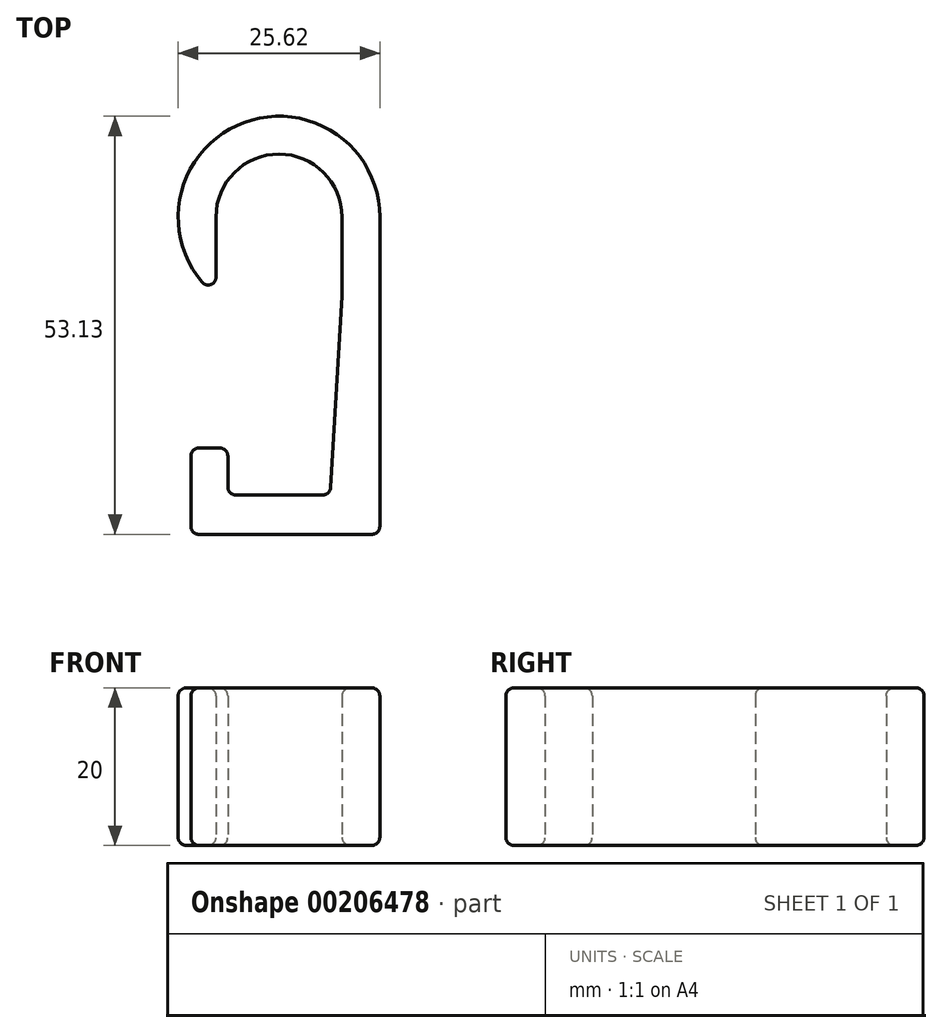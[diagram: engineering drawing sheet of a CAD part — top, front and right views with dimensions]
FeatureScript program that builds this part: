
annotation { "Feature Type Name" : "Feature", "Feature Type Description" : "" }
export const myFeature = defineFeature(function(context is Context, id is Id, definition is map)
    precondition{}
    {
        {
            var Q0;
            Q0=qCreatedBy(makeId("Top.planeOp"),FACE);
            var sketch = newSketch(context, id + "F0", { "sketchPlane" : qUnion([Q0])});
            skArc(sketch, "E0", {"start": v(8, 0) * mm, "mid": v(0, 8) * mm, "end": v(-8, 0) * mm});
            skArc(sketch, "E1", {"start": v(12.8, 0) * mm, "mid": v(-5.55, 11.54) * mm, "end": v(-8, -10) * mm});
            skLineSegment(sketch, "E2", {"start": v(-8, 0) * mm, "end": v(-8, -10) * mm});
            skLineSegment(sketch, "E3", {"start": v(8, 0) * mm, "end": v(8, -10) * mm});
            skLineSegment(sketch, "E4", {"start": v(0, -35.32) * mm, "end": v(6.5, -35.32) * mm});
            skLineSegment(sketch, "E5", {"start": v(0, -35.32) * mm, "end": v(-6.5, -35.32) * mm});
            skLineSegment(sketch, "E6", {"start": v(8, -10) * mm, "end": v(6.5, -35.32) * mm});
            skLineSegment(sketch, "E7", {"start": v(12.8, 0) * mm, "end": v(12.8, -40.32) * mm});
            skLineSegment(sketch, "E8", {"start": v(12.8, -40.32) * mm, "end": v(-11.2, -40.32) * mm});
            skLineSegment(sketch, "E9", {"start": v(-11.2, -29.34) * mm, "end": v(-6.5, -29.34) * mm});
            skLineSegment(sketch, "E10", {"start": v(-6.5, -29.34) * mm, "end": v(-6.5, -35.32) * mm});
            skLineSegment(sketch, "E11", {"start": v(-11.2, -40.32) * mm, "end": v(-11.2, -29.34) * mm});
            skSolve(sketch);
        }
        {
            var Q0;
            Q0=makeQuery(id+"F0.imprint","IMPRINT",FACE,{"disambiguationData":[TD([[makeQuery(id+"F0.imprint","IMPRINT",EDGE,{"derivedFrom":sQuery(id+"F0.wireOp",EDGE,"E0")}),-1.0]])]});
            extrude(context, id + "F1", {"entities" : qUnion([Q0]), "depth" : 20 * mm});
        }
        {
            var Q0;
            Q0=makeQuery(id+"F1.opExtrude","CAP_FACE",FACE,{"disambiguationData":[OSD([sQuery(id+"F0.wireOp",EDGE,"E0"),sQuery(id+"F0.wireOp",EDGE,"E1"),sQuery(id+"F0.wireOp",EDGE,"E2"),sQuery(id+"F0.wireOp",EDGE,"E3"),sQuery(id+"F0.wireOp",EDGE,"E4"),sQuery(id+"F0.wireOp",EDGE,"E5"),sQuery(id+"F0.wireOp",EDGE,"E6"),sQuery(id+"F0.wireOp",EDGE,"E7"),sQuery(id+"F0.wireOp",EDGE,"E8"),sQuery(id+"F0.wireOp",EDGE,"E9"),sQuery(id+"F0.wireOp",EDGE,"E10"),sQuery(id+"F0.wireOp",EDGE,"E11")])],"isStart":false});
            var Q1;
            Q1=makeQuery(id+"F1.opExtrude","CAP_EDGE",EDGE,{"disambiguationData":[OSD([sQuery(id+"F0.wireOp",EDGE,"E1")])],"isStart":true});
            var Q2;
            Q2=makeQuery(id+"F1.opExtrude","CAP_EDGE",EDGE,{"disambiguationData":[OSD([sQuery(id+"F0.wireOp",EDGE,"E1")])],"isStart":false});
            var Q3;
            Q3=makeQuery(id+"F1.opExtrude","SWEPT_EDGE",EDGE,{"disambiguationData":[OSD([sQuery(id+"F0.wireOp",EDGE,"E0"),sQuery(id+"F0.wireOp",EDGE,"E2")])]});
            var Q4;
            Q4=makeQuery(id+"F1.opExtrude","SWEPT_EDGE",EDGE,{"disambiguationData":[OSD([sQuery(id+"F0.wireOp",EDGE,"E1"),sQuery(id+"F0.wireOp",EDGE,"E7")])]});
            var Q5;
            Q5=makeQuery(id+"F1.opExtrude","SWEPT_EDGE",EDGE,{"disambiguationData":[OSD([sQuery(id+"F0.wireOp",EDGE,"E1"),sQuery(id+"F0.wireOp",EDGE,"E2")])]});
            var Q6;
            Q6=makeQuery(id+"F1.opExtrude","SWEPT_EDGE",EDGE,{"disambiguationData":[OSD([sQuery(id+"F0.wireOp",EDGE,"E7"),sQuery(id+"F0.wireOp",EDGE,"E8")])]});
            var Q7;
            Q7=makeQuery(id+"F1.opExtrude","SWEPT_EDGE",EDGE,{"disambiguationData":[OSD([sQuery(id+"F0.wireOp",EDGE,"E8"),sQuery(id+"F0.wireOp",EDGE,"E11")])]});
            var Q8;
            Q8=makeQuery(id+"F1.opExtrude","SWEPT_EDGE",EDGE,{"disambiguationData":[OSD([sQuery(id+"F0.wireOp",EDGE,"E9"),sQuery(id+"F0.wireOp",EDGE,"E10")])]});
            var Q9;
            Q9=makeQuery(id+"F1.opExtrude","CAP_EDGE",EDGE,{"disambiguationData":[OSD([sQuery(id+"F0.wireOp",EDGE,"E10")])],"isStart":false});
            var Q10;
            Q10=makeQuery(id+"F1.opExtrude","CAP_EDGE",EDGE,{"disambiguationData":[OSD([sQuery(id+"F0.wireOp",EDGE,"E2")])],"isStart":false});
            var Q11;
            Q11=makeQuery(id+"F1.opExtrude","CAP_EDGE",EDGE,{"disambiguationData":[OSD([sQuery(id+"F0.wireOp",EDGE,"E11")])],"isStart":false});
            var Q12;
            Q12=makeQuery(id+"F1.opExtrude","CAP_EDGE",EDGE,{"disambiguationData":[OSD([sQuery(id+"F0.wireOp",EDGE,"E3")])],"isStart":false});
            var Q13;
            Q13=makeQuery(id+"F1.opExtrude","CAP_EDGE",EDGE,{"disambiguationData":[OSD([sQuery(id+"F0.wireOp",EDGE,"E6")])],"isStart":false});
            var Q14;
            Q14=makeQuery(id+"F1.opExtrude","CAP_EDGE",EDGE,{"disambiguationData":[OSD([sQuery(id+"F0.wireOp",EDGE,"E7")])],"isStart":true});
            var Q15;
            Q15=makeQuery(id+"F1.opExtrude","CAP_EDGE",EDGE,{"disambiguationData":[OSD([sQuery(id+"F0.wireOp",EDGE,"E7")])],"isStart":false});
            var Q16;
            Q16=makeQuery(id+"F1.opExtrude","CAP_EDGE",EDGE,{"disambiguationData":[OSD([sQuery(id+"F0.wireOp",EDGE,"E8")])],"isStart":false});
            var Q17;
            Q17=makeQuery(id+"F1.opExtrude","CAP_EDGE",EDGE,{"disambiguationData":[OSD([sQuery(id+"F0.wireOp",EDGE,"E9")])],"isStart":false});
            var Q18;
            Q18=makeQuery(id+"F1.opExtrude","CAP_EDGE",EDGE,{"disambiguationData":[OSD([sQuery(id+"F0.wireOp",EDGE,"E2")])],"isStart":true});
            var Q19;
            Q19=makeQuery(id+"F1.opExtrude","SWEPT_EDGE",EDGE,{"disambiguationData":[OSD([sQuery(id+"F0.wireOp",EDGE,"E0"),sQuery(id+"F0.wireOp",EDGE,"E3")])]});
            var Q20;
            Q20=makeQuery(id+"F1.opExtrude","SWEPT_EDGE",EDGE,{"disambiguationData":[OSD([sQuery(id+"F0.wireOp",EDGE,"E3"),sQuery(id+"F0.wireOp",EDGE,"E6")])]});
            var Q21;
            Q21=makeQuery(id+"F1.opExtrude","SWEPT_EDGE",EDGE,{"disambiguationData":[OSD([sQuery(id+"F0.wireOp",EDGE,"E4"),sQuery(id+"F0.wireOp",EDGE,"E6")])]});
            var Q22;
            Q22=makeQuery(id+"F1.opExtrude","SWEPT_EDGE",EDGE,{"disambiguationData":[OSD([sQuery(id+"F0.wireOp",EDGE,"E5"),sQuery(id+"F0.wireOp",EDGE,"E10")])]});
            var Q23;
            Q23=makeQuery(id+"F1.opExtrude","SWEPT_EDGE",EDGE,{"disambiguationData":[OSD([sQuery(id+"F0.wireOp",EDGE,"E9"),sQuery(id+"F0.wireOp",EDGE,"E11")])]});
            var Q24;
            Q24=makeQuery(id+"F1.opExtrude","CAP_EDGE",EDGE,{"disambiguationData":[OSD([sQuery(id+"F0.wireOp",EDGE,"E0")])],"isStart":true});
            var Q25;
            Q25=makeQuery(id+"F1.opExtrude","CAP_EDGE",EDGE,{"disambiguationData":[OSD([sQuery(id+"F0.wireOp",EDGE,"E0")])],"isStart":false});
            var Q26;
            Q26=makeQuery(id+"F1.opExtrude","CAP_EDGE",EDGE,{"disambiguationData":[OSD([sQuery(id+"F0.wireOp",EDGE,"E10")])],"isStart":true});
            var Q27;
            Q27=makeQuery(id+"F1.opExtrude","CAP_EDGE",EDGE,{"disambiguationData":[OSD([sQuery(id+"F0.wireOp",EDGE,"E11")])],"isStart":true});
            var Q28;
            Q28=makeQuery(id+"F1.opExtrude","CAP_EDGE",EDGE,{"disambiguationData":[OSD([sQuery(id+"F0.wireOp",EDGE,"E3")])],"isStart":true});
            var Q29;
            Q29=makeQuery(id+"F1.opExtrude","CAP_EDGE",EDGE,{"disambiguationData":[OSD([sQuery(id+"F0.wireOp",EDGE,"E4"),sQuery(id+"F0.wireOp",EDGE,"E5")])],"isStart":true});
            var Q30;
            Q30=makeQuery(id+"F1.opExtrude","CAP_EDGE",EDGE,{"disambiguationData":[OSD([sQuery(id+"F0.wireOp",EDGE,"E4"),sQuery(id+"F0.wireOp",EDGE,"E5")])],"isStart":false});
            var Q31;
            Q31=makeQuery(id+"F1.opExtrude","CAP_EDGE",EDGE,{"disambiguationData":[OSD([sQuery(id+"F0.wireOp",EDGE,"E6")])],"isStart":true});
            var Q32;
            Q32=makeQuery(id+"F1.opExtrude","CAP_EDGE",EDGE,{"disambiguationData":[OSD([sQuery(id+"F0.wireOp",EDGE,"E8")])],"isStart":true});
            var Q33;
            Q33=makeQuery(id+"F1.opExtrude","CAP_EDGE",EDGE,{"disambiguationData":[OSD([sQuery(id+"F0.wireOp",EDGE,"E9")])],"isStart":true});
            fillet(context, id + "F2", {"entities" : qUnion([Q0, Q1, Q2, Q3, Q4, Q5, Q6, Q7, Q8, Q9, Q10, Q11, Q12, Q13, Q14, Q15, Q16, Q17, Q18, Q19, Q20, Q21, Q22, Q23, Q24, Q25, Q26, Q27, Q28, Q29, Q30, Q31, Q32, Q33]), "radius" : 1 * mm, "tangentPropagation" : true, "allowEdgeOverflow" : false});
        }
    });
